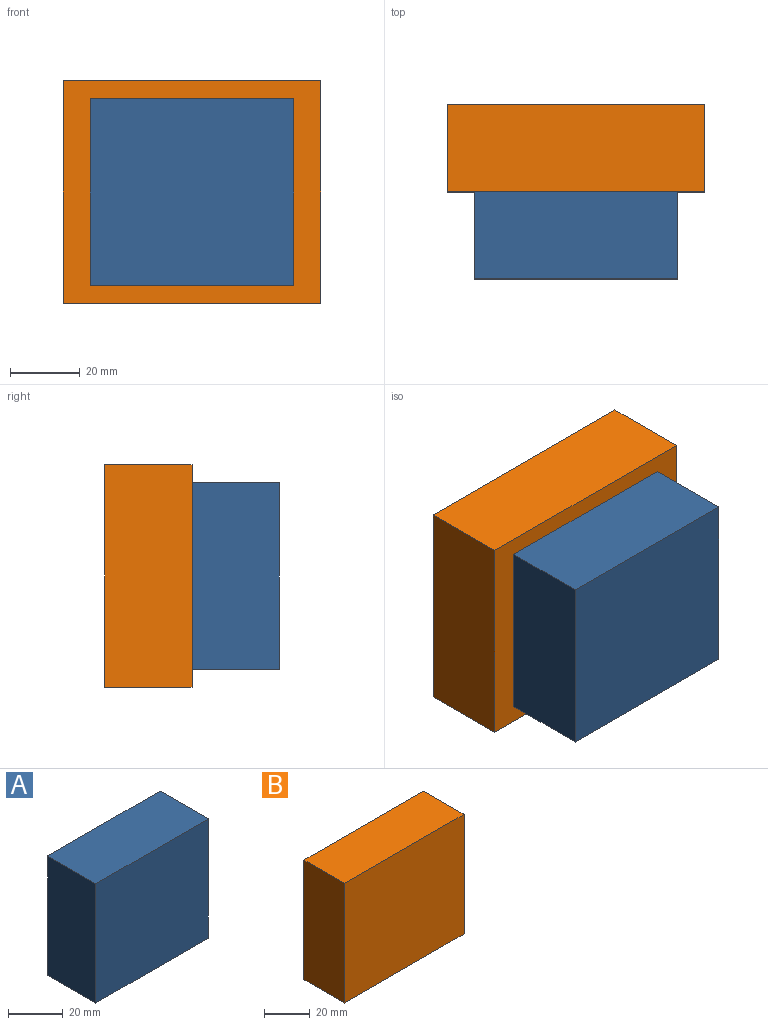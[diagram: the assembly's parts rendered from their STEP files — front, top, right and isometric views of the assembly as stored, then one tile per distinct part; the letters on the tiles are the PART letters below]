
ASSEMBLY  parts=2 mates=1
PART A: 6 faces, bbox 58.3x25x53.5 mm
  f0: plane 58.34x25mm, normal (0,0,1), area 1458.4mm2, adj f1,f3,f4,f5
  f1: plane 53.52x25mm, normal (-1,0,0), area 1337.9mm2, adj f0,f2,f4,f5
  f2: plane 58.34x25mm, normal (0,0,-1), area 1458.4mm2, adj f1,f3,f4,f5
  f3: plane 53.52x25mm, normal (1,0,0), area 1337.9mm2, adj f0,f2,f4,f5
  f4: plane 58.34x53.52mm, normal (0,-1,0), area 3121.9mm2, adj f0,f1,f2,f3
  f5: plane 58.34x53.52mm, normal (0,1,0), area 3121.9mm2, adj f0,f1,f2,f3
PART B: 6 faces, bbox 73.9x25x64 mm
  f0: plane 73.87x25mm, normal (0,0,1), area 1846.8mm2, adj f1,f3,f4,f5
  f1: plane 63.98x25mm, normal (-1,0,0), area 1599.5mm2, adj f0,f2,f4,f5
  f2: plane 73.87x25mm, normal (0,0,-1), area 1846.8mm2, adj f1,f3,f4,f5
  f3: plane 63.98x25mm, normal (1,0,0), area 1599.5mm2, adj f0,f2,f4,f5
  f4: plane 73.87x63.98mm, normal (0,-1,0), area 4726.5mm2, adj f0,f1,f2,f3
  f5: plane 73.87x63.98mm, normal (0,1,0), area 4726.5mm2, adj f0,f1,f2,f3
PLACE A rot(axis=(1,0,0),180deg) t=(-19.64,-52.52,49.76)mm
PLACE B t=(102.75,-2.52,43.78)mm
MATE fastened A.f4 <-> B.f4  axis (0,1,0) through (-12.31,-27.52,-11.86)mm
